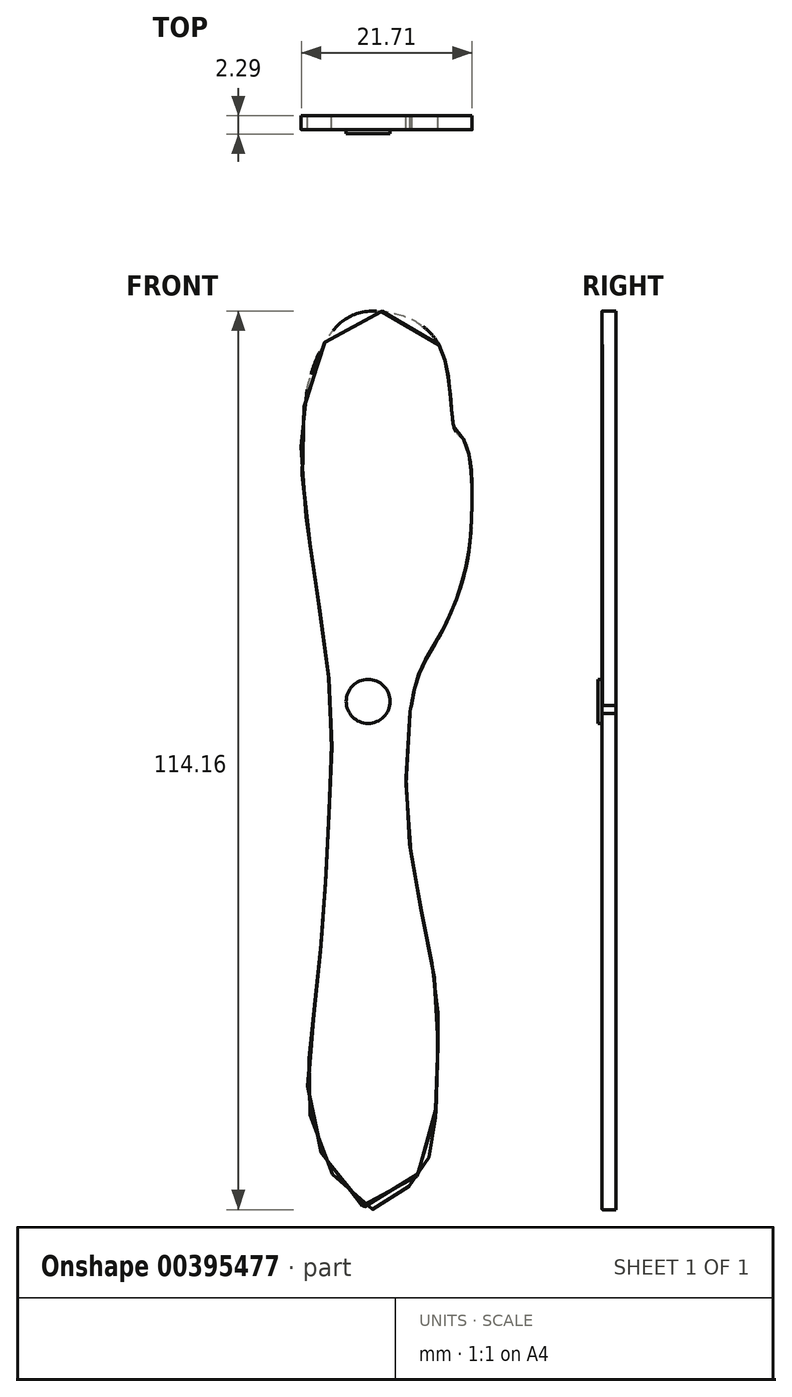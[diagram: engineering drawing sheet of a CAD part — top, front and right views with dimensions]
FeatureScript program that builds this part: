
annotation { "Feature Type Name" : "Feature", "Feature Type Description" : "" }
export const myFeature = defineFeature(function(context is Context, id is Id, definition is map)
    precondition{}
    {
        {
            var Q0;
            Q0=qCreatedBy(makeId("Front.planeOp"),FACE);
            var sketch = newSketch(context, id + "F0", { "sketchPlane" : qUnion([Q0])});
            skLineSegment(sketch, "E0", {"start": v(0, 76) * mm, "end": v(0, -76.72) * mm, "construction": true});
            skFitSpline(sketch, "E1", {"points": [v(-8.5, 60.45) * mm, v(-4.95, 67.5) * mm, v(0, 69.44) * mm, v(8.03, 65.15) * mm, v(10.09, 54.27) * mm, v(11.31, 52.96) * mm, v(12.21, 43.54) * mm, v(10.85, 34.59) * mm, v(7.78, 27.55) * mm, v(5.17, 22.34) * mm, v(3.98, 5.65) * mm, v(6.12, -8.23) * mm, v(7.8, -18.2) * mm, v(7.8, -27.89) * mm, v(7.08, -37.1) * mm, v(5.43, -40.16) * mm, v(0, -44.72) * mm, v(-7.55, -35.91) * mm, v(-8.26, -23.4) * mm, v(-6.85, -9.7) * mm, v(-5.9, 6.12) * mm, v(-5.9, 21.94) * mm, v(-9.2, 46.73) * mm, v(-8.5, 60.45) * mm]});
            skFitSpline(sketch, "E2", {"points": [v(8.03, 65.15) * mm, v(13.7, 54.27) * mm, v(15.82, 43.66) * mm, v(14.64, 33.98) * mm, v(10.85, 26.66) * mm, v(7.78, 22.34) * mm, v(4.36, 18.32) * mm], "startDerivative": vector(52.75, -63.3) * mm, "endDerivative": vector(0, -52.92) * mm});
            skSolve(sketch);
        }
        {
            var Q0;
            Q0=makeQuery(id+"F0.imprint","IMPRINT",FACE,{"disambiguationData":[TD([[makeQuery(id+"F0.imprint","IMPRINT",EDGE,{"derivedFrom":sQuery(id+"F0.wireOp",EDGE,"E1")}),-1.0]])]});
            extrude(context, id + "F1", {"entities" : qUnion([Q0]), "depth" : 1.78 * mm});
        }
        {
            var Q0;
            Q0=makeQuery(id+"F1.opExtrude","CAP_EDGE",EDGE,{"disambiguationData":[OSD([sQuery(id+"F0.wireOp",EDGE,"E1")])],"isStart":false});
            fillet(context, id + "F2", {"entities" : qUnion([Q0]), "radius" : 0.03 * mm, "tangentPropagation" : true, "allowEdgeOverflow" : false});
        }
        {
            var Q0;
            Q0=makeQuery(id+"F1.opExtrude","CAP_FACE",FACE,{"disambiguationData":[OSD([sQuery(id+"F0.wireOp",EDGE,"E1"),sQuery(id+"F0.wireOp",EDGE,"E2")])],"isStart":false});
            var sketch = newSketch(context, id + "F3", { "sketchPlane" : qUnion([Q0])});
            skCircle(sketch, "E3", {"center": v(-0.96, 19.85) * mm, "radius": 2.8 * mm});
            skSolve(sketch);
        }
        {
            var Q0;
            Q0=makeQuery(id+"F3.imprint","IMPRINT",FACE,{"disambiguationData":[TD([[makeQuery(id+"F3.imprint","IMPRINT",EDGE,{"derivedFrom":sQuery(id+"F3.wireOp",EDGE,"E3")}),1.0]])]});
            extrude(context, id + "F4", {"entities" : qUnion([Q0]), "operationType" : NewBodyOperationType.ADD, "depth" : 0.5 * mm});
        }
    });
